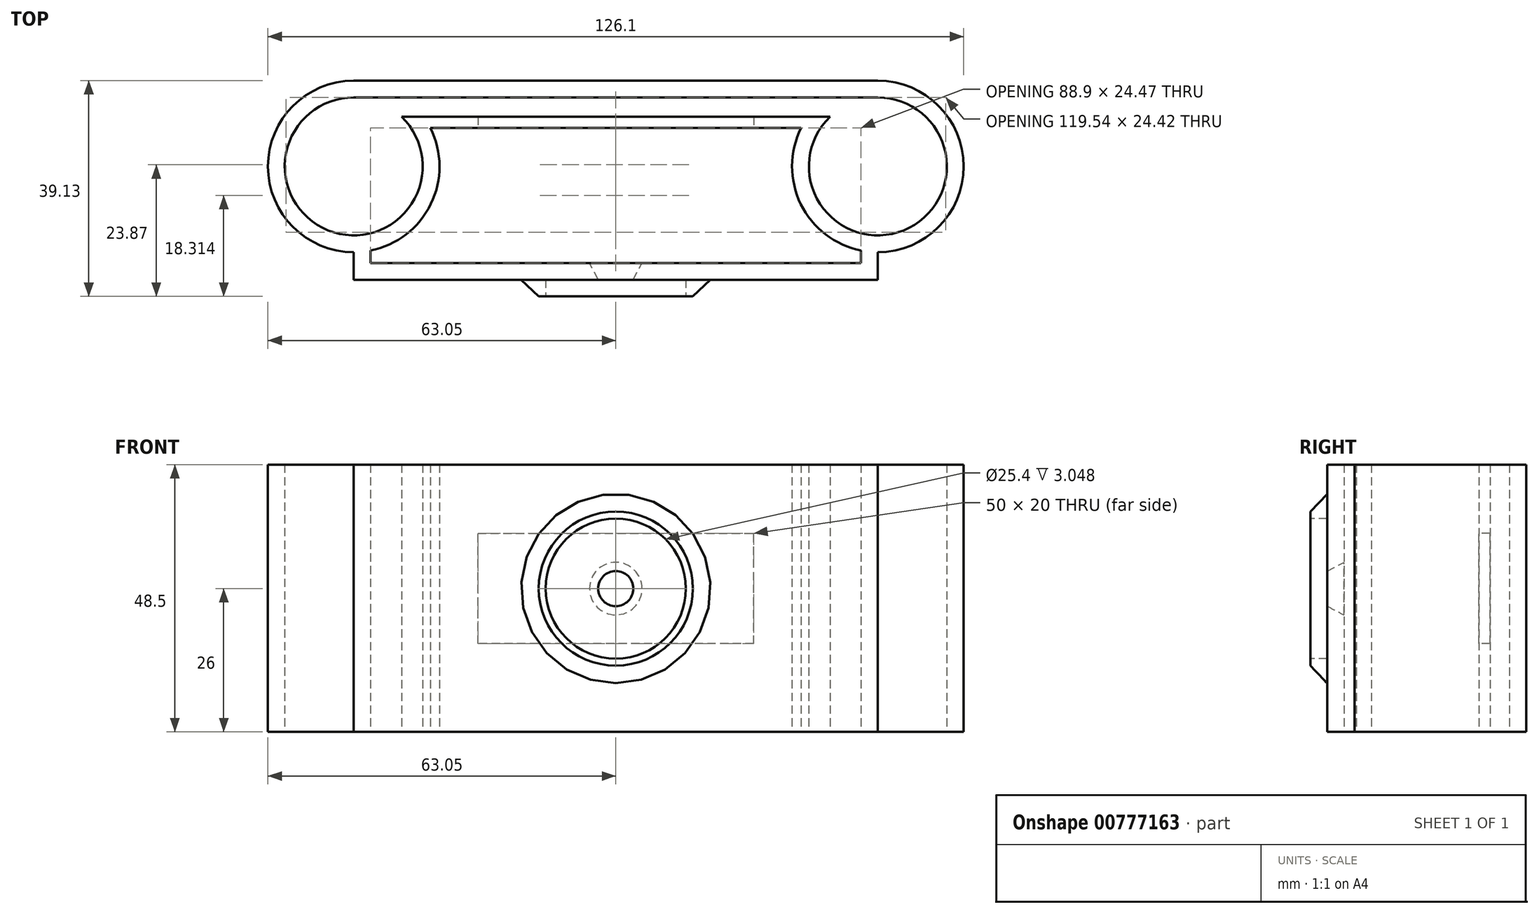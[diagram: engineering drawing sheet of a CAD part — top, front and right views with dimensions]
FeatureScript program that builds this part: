
annotation { "Feature Type Name" : "Feature", "Feature Type Description" : "" }
export const myFeature = defineFeature(function(context is Context, id is Id, definition is map)
    precondition{}
    {
        {
            var Q0;
            Q0=qCreatedBy(makeId("Top.planeOp"),FACE);
            var sketch = newSketch(context, id + "F0", { "sketchPlane" : qUnion([Q0])});
            skLineSegment(sketch, "E0.bottom", {"start": v(44.45, 15) * mm, "end": v(38.25, 15) * mm});
            skLineSegment(sketch, "E0.top", {"start": v(44.45, -15) * mm, "end": v(-44.45, -15) * mm});
            skLineSegment(sketch, "E0.left", {"start": v(44.45, 15) * mm, "end": v(44.45, -15) * mm});
            skLineSegment(sketch, "E0.right", {"start": v(-44.45, 15) * mm, "end": v(-44.45, -15) * mm});
            skPoint(sketch, "E0.middle", {"position": v(0, 0) * mm});
            skLineSegment(sketch, "E1.0", {"start": v(47.5, 18.05) * mm, "end": v(-47.5, 18.05) * mm});
            skLineSegment(sketch, "E1.1", {"start": v(47.5, 18.05) * mm, "end": v(47.5, 15) * mm});
            skLineSegment(sketch, "E1.2", {"start": v(47.5, -18.05) * mm, "end": v(-47.5, -18.05) * mm});
            skLineSegment(sketch, "E1.3", {"start": v(-47.5, 18.05) * mm, "end": v(-47.5, -18.05) * mm});
            skLineSegment(sketch, "E2", {"start": v(38.25, 15) * mm, "end": v(-44.45, 15) * mm});
            skArc(sketch, "E3", {"start": v(34.82, 11.5) * mm, "mid": v(58.6, -8.39) * mm, "end": v(38.25, 15) * mm});
            skLineSegment(sketch, "E4", {"start": v(47.5, 15) * mm, "end": v(47.5, -18.05) * mm});
            skArc(sketch, "E5", {"start": v(38.82, 11.5) * mm, "mid": v(52.18, -9.1) * mm, "end": v(47.5, 15) * mm});
            skLineSegment(sketch, "E6", {"start": v(38.82, 11.5) * mm, "end": v(34.82, 11.5) * mm});
            skLineSegment(sketch, "E7", {"start": v(47.5, 15) * mm, "end": v(44.45, 15) * mm});
            skArc(sketch, "E8", {"start": v(-38.25, 15) * mm, "mid": v(-58.6, -8.39) * mm, "end": v(-34.82, 11.5) * mm});
            skArc(sketch, "E9", {"start": v(-47.5, 15) * mm, "mid": v(-52.18, -9.1) * mm, "end": v(-38.82, 11.5) * mm});
            skLineSegment(sketch, "E10", {"start": v(-38.82, 11.5) * mm, "end": v(-34.82, 11.5) * mm});
            skLineSegment(sketch, "E11", {"start": v(-47.5, 15) * mm, "end": v(-44.45, 15) * mm});
            skLineSegment(sketch, "E12", {"start": v(-34.82, 11.5) * mm, "end": v(34.82, 11.5) * mm});
            skLineSegment(sketch, "E13", {"start": v(34.82, 9.46) * mm, "end": v(-34.82, 9.47) * mm});
            skLineSegment(sketch, "E14", {"start": v(-34.82, 9.47) * mm, "end": v(-34.82, 11.5) * mm});
            skLineSegment(sketch, "E15", {"start": v(34.82, 11.5) * mm, "end": v(34.82, 9.46) * mm});
            skSolve(sketch);
        }
        {
            var Q0;
            Q0=qSketchRegion(id+"F0",true);
            var Q1;
            {var subQ0=sQuery(id+"F0.wireOp",EDGE,"E10");Q1=makeQuery(id+"F0.imprint","IMPRINT",FACE,{"disambiguationData":[TD([[makeQuery(id+"F0.imprint","IMPRINT",EDGE,{"derivedFrom":subQ0}),-1.0]])]});}
            var Q2;
            {var subQ0=sQuery(id+"F0.wireOp",EDGE,"E12");Q2=makeQuery(id+"F0.imprint","IMPRINT",FACE,{"disambiguationData":[TD([[makeQuery(id+"F0.imprint","IMPRINT",EDGE,{"derivedFrom":subQ0}),-1.0]])]});}
            var Q3;
            {var subQ0=sQuery(id+"F0.wireOp",EDGE,"E14");Q3=makeQuery(id+"F0.imprint","IMPRINT",FACE,{"disambiguationData":[TD([[makeQuery(id+"F0.imprint","IMPRINT",EDGE,{"derivedFrom":subQ0}),-1.0]])]});}
            var Q4;
            {var subQ0=sQuery(id+"F0.wireOp",EDGE,"E15");Q4=makeQuery(id+"F0.imprint","IMPRINT",FACE,{"disambiguationData":[TD([[makeQuery(id+"F0.imprint","IMPRINT",EDGE,{"derivedFrom":subQ0}),-1.0]])]});}
            var Q5;
            {var subQ0=sQuery(id+"F0.wireOp",EDGE,"E6");Q5=makeQuery(id+"F0.imprint","IMPRINT",FACE,{"disambiguationData":[TD([[makeQuery(id+"F0.imprint","IMPRINT",EDGE,{"derivedFrom":subQ0}),1.0]])]});}
            extrude(context, id + "F1", {"entities" : qUnion([Q0, Q1, Q2, Q3, Q4, Q5]), "endBound" : BoundingType.SYMMETRIC, "depth" : 48.5 * mm, "offsetDistance" : 25.4 * mm});
        }
        {
            var Q0;
            Q0=qCreatedBy(makeId("Front.planeOp"),FACE);
            cPlane(context, id + "F2", {"entities" : qUnion([Q0]), "cplaneType" : CPlaneType.OFFSET, "offset" : 18.05 * mm, "width" : 152.4 * mm, "height" : 152.4 * mm});
        }
        {
            var Q0;
            Q0=qCreatedBy(makeId("Front.planeOp"),FACE);
            cPlane(context, id + "F3", {"entities" : qUnion([Q0]), "cplaneType" : CPlaneType.OFFSET, "offset" : 15 * mm, "width" : 152.4 * mm, "height" : 152.4 * mm});
        }
        {
            var Q0;
            Q0=qCreatedBy(id+"F3.planeOp",FACE);
            var sketch = newSketch(context, id + "F4", { "sketchPlane" : qUnion([Q0])});
            skCircle(sketch, "E16", {"center": v(0, 1.75) * mm, "radius": 4.76 * mm});
            skSolve(sketch);
        }
        {
            var Q0;
            Q0=qCreatedBy(id+"F2.planeOp",FACE);
            var sketch = newSketch(context, id + "F5", { "sketchPlane" : qUnion([Q0])});
            skCircle(sketch, "E17", {"center": v(0, 1.75) * mm, "radius": 3.18 * mm});
            skSolve(sketch);
        }
        {
            var Q1;
            Q1=qSketchRegion(id+"F5",true);
            var Q2;
            Q2=qSketchRegion(id+"F4",true);
            loft(context, id + "F6", {"operationType" : NewBodyOperationType.REMOVE, "sheetProfilesArray" : [{ "sheetProfileEntities" : qUnion([Q1]) }, { "sheetProfileEntities" : qUnion([Q2]) }]});
        }
        {
            var Q0;
            Q0=qCreatedBy(id+"F2.planeOp",FACE);
            var sketch = newSketch(context, id + "F7", { "sketchPlane" : qUnion([Q0])});
            skCircle(sketch, "E18", {"center": v(0, 1.75) * mm, "radius": 17.15 * mm});
            skSolve(sketch);
        }
        {
            var Q0;
            Q0=qCreatedBy(makeId("Front.planeOp"),FACE);
            cPlane(context, id + "F8", {"entities" : qUnion([Q0]), "cplaneType" : CPlaneType.OFFSET, "offset" : 21.08 * mm, "width" : 152.4 * mm, "height" : 152.4 * mm});
        }
        {
            var Q0;
            Q0=qCreatedBy(makeId("Front.planeOp"),FACE);
            cPlane(context, id + "F9", {"entities" : qUnion([Q0]), "cplaneType" : CPlaneType.OFFSET, "offset" : 9.46 * mm, "oppositeDirection" : true, "width" : 152.4 * mm, "height" : 152.4 * mm});
        }
        {
            var Q0;
            Q0=qCreatedBy(id+"F9.planeOp",FACE);
            var sketch = newSketch(context, id + "F10", { "sketchPlane" : qUnion([Q0])});
            skPoint(sketch, "E19.middle", {"position": v(0, 0) * mm});
            skLineSegment(sketch, "E20.bottom", {"start": v(25, -8.25) * mm, "end": v(-25, -8.25) * mm});
            skLineSegment(sketch, "E20.top", {"start": v(25, 11.75) * mm, "end": v(-25, 11.75) * mm});
            skLineSegment(sketch, "E20.left", {"start": v(25, -8.25) * mm, "end": v(25, 11.75) * mm});
            skLineSegment(sketch, "E20.right", {"start": v(-25, -8.25) * mm, "end": v(-25, 11.75) * mm});
            skSolve(sketch);
        }
        {
            var Q0;
            Q0=qSketchRegion(id+"F10",true);
            extrude(context, id + "F11", {"entities" : qUnion([Q0]), "operationType" : NewBodyOperationType.REMOVE, "oppositeDirection" : true, "depth" : 2.03 * mm, "offsetDistance" : 25.4 * mm});
        }
        {
            var Q0;
            Q0=qCreatedBy(id+"F8.planeOp",FACE);
            var sketch = newSketch(context, id + "F12", { "sketchPlane" : qUnion([Q0])});
            skCircle(sketch, "E21", {"center": v(0, 1.75) * mm, "radius": 13.97 * mm});
            skSolve(sketch);
        }
        {
            var Q1;
            Q1=makeQuery(id+"F7.imprint","IMPRINT",FACE,{"disambiguationData":[TD([[makeQuery(id+"F7.imprint","IMPRINT",EDGE,{"derivedFrom":sQuery(id+"F7.wireOp",EDGE,"E18")}),1.0]])]});
            var Q2;
            Q2=makeQuery(id+"F12.imprint","IMPRINT",FACE,{"disambiguationData":[TD([[makeQuery(id+"F12.imprint","IMPRINT",EDGE,{"derivedFrom":sQuery(id+"F12.wireOp",EDGE,"E21")}),1.0]])]});
            loft(context, id + "F13", {"operationType" : NewBodyOperationType.ADD, "sheetProfilesArray" : [{ "sheetProfileEntities" : qUnion([Q1]) }, { "sheetProfileEntities" : qUnion([Q2]) }]});
        }
        {
            var Q0;
            Q0=qCreatedBy(id+"F8.planeOp",FACE);
            var sketch = newSketch(context, id + "F14", { "sketchPlane" : qUnion([Q0])});
            skCircle(sketch, "E22", {"center": v(0, 1.75) * mm, "radius": 12.7 * mm});
            skSolve(sketch);
        }
        {
            var Q0;
            Q0=qSketchRegion(id+"F14",true);
            extrude(context, id + "F15", {"entities" : qUnion([Q0]), "operationType" : NewBodyOperationType.REMOVE, "oppositeDirection" : true, "depth" : 3.05 * mm, "offsetDistance" : 25.4 * mm});
        }
    });
